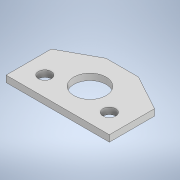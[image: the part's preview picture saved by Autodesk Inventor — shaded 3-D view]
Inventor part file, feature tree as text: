
AUTODESK INVENTOR PART (.ipt)
format: ipt  version: 2022.2 (Build 262287030, 287C)  size: 114,688 bytes
history: native  units: in
note: dims shown in document units (in); Inventor stores cm internally (conversion verified against a paired STEP export)
features: extrude x1, sketch x1
ambient origin geometry x8: Origin, YZ Plane, XZ Plane, XY Plane, X Axis, Y Axis, Z Axis, Center Point
bodies: Solid1 (feature_tree)
feature tree (2):
  extrude  "Extrusion1"  Depth=0.25in
  sketch  "Sketch1"  dims[d6=4.0in d7=0.75in d8=0.75in d9=1.25in d10=1.25in d11=2.5in d12=1.75in d13=0.5in d14=1.25in d15=0.25in d16=0.0in]
